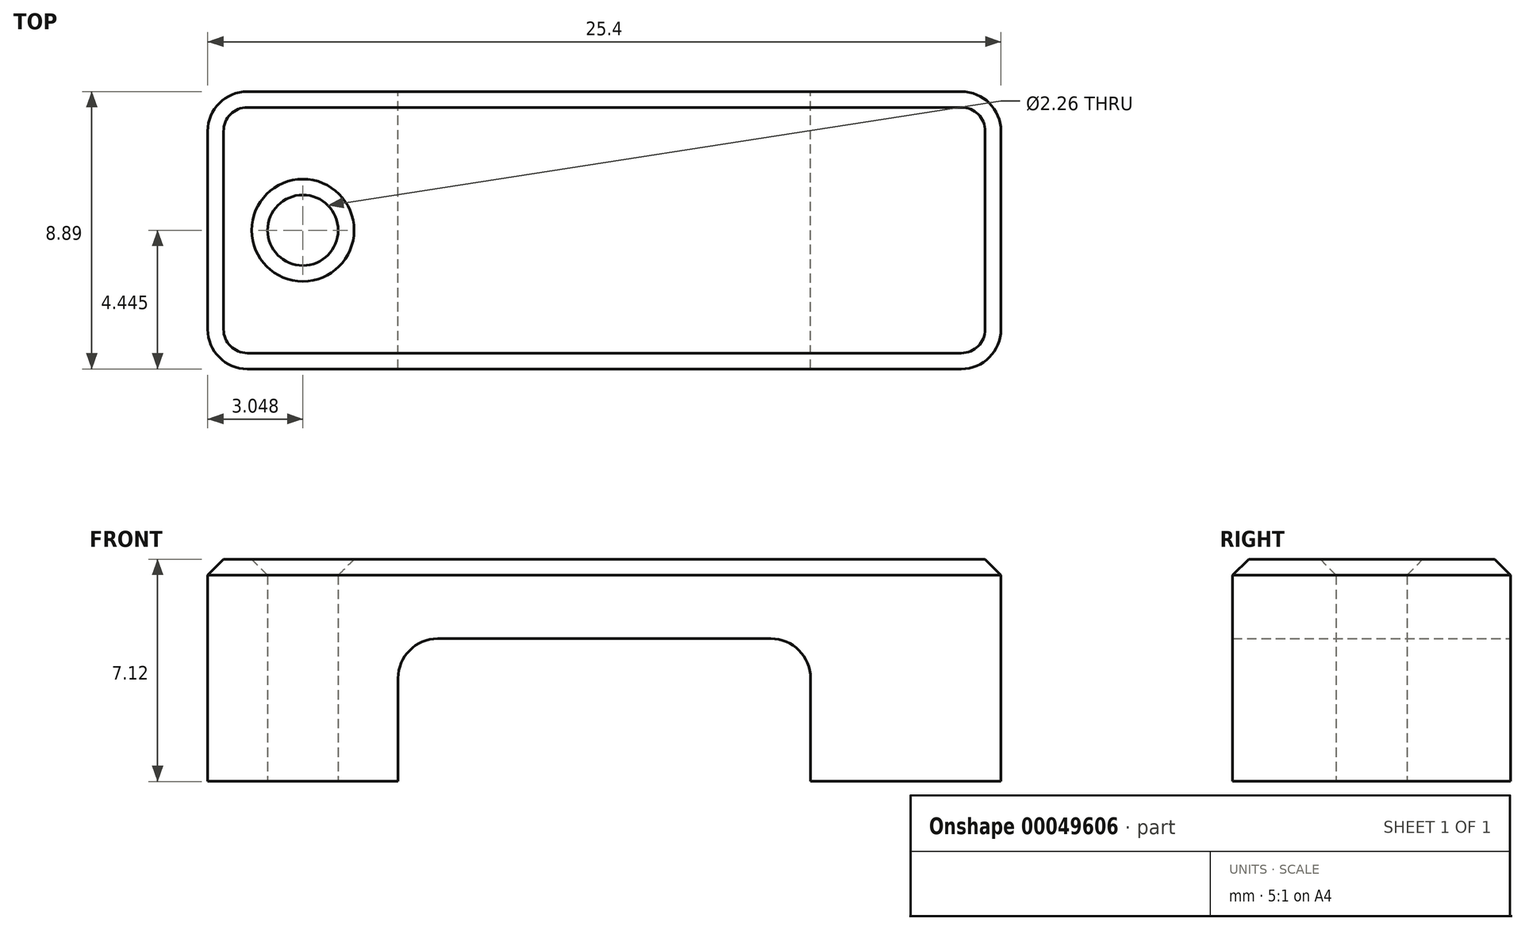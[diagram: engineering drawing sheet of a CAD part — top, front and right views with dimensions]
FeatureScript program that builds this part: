
annotation { "Feature Type Name" : "Feature", "Feature Type Description" : "" }
export const myFeature = defineFeature(function(context is Context, id is Id, definition is map)
    precondition{}
    {
        {
            var Q0;
            Q0=qCreatedBy(makeId("Front.planeOp"),FACE);
            var sketch = newSketch(context, id + "F0", { "sketchPlane" : qUnion([Q0])});
            skLineSegment(sketch, "E0.rect.bottom", {"start": v(6.6, 2.29) * mm, "end": v(-6.6, 2.29) * mm});
            skLineSegment(sketch, "E0.rect.left", {"start": v(6.6, 2.29) * mm, "end": v(6.6, -2.29) * mm});
            skLineSegment(sketch, "E0.rect.right", {"start": v(-6.6, 2.29) * mm, "end": v(-6.6, -2.29) * mm});
            skPoint(sketch, "E0.rect.middle", {"position": v(0, 0) * mm});
            skLineSegment(sketch, "E1.bottom", {"start": v(-12.7, -2.29) * mm, "end": v(-6.6, -2.29) * mm});
            skLineSegment(sketch, "E1.top", {"start": v(-12.7, 4.83) * mm, "end": v(12.7, 4.83) * mm});
            skLineSegment(sketch, "E1.left", {"start": v(-12.7, -2.29) * mm, "end": v(-12.7, 4.83) * mm});
            skLineSegment(sketch, "E1.right", {"start": v(12.7, -2.29) * mm, "end": v(12.7, 4.83) * mm});
            skLineSegment(sketch, "E2.trimOffspring", {"start": v(6.6, -2.29) * mm, "end": v(12.7, -2.29) * mm});
            skSolve(sketch);
        }
        {
            var Q0;
            Q0=makeQuery(id+"F0.imprint","IMPRINT",FACE,{"disambiguationData":[TD([[makeQuery(id+"F0.imprint","IMPRINT",EDGE,{"derivedFrom":sQuery(id+"F0.wireOp",EDGE,"E0.rect.bottom")}),-1.0]])]});
            extrude(context, id + "F1", {"entities" : qUnion([Q0]), "depth" : 8.9 * mm});
        }
        {
            var Q0;
            Q0=makeQuery(id+"F1.opExtrude","SWEPT_FACE",FACE,{"disambiguationData":[OSD([sQuery(id+"F0.wireOp",EDGE,"E1.bottom")])]});
            var sketch = newSketch(context, id + "F2", { "sketchPlane" : qUnion([Q0])});
            skCircle(sketch, "E3", {"center": v(-9.65, 4.45) * mm, "radius": 1.13 * mm});
            skPoint(sketch, "E3.centerSnap0", {"position": v(-12.7, 4.45) * mm});
            skPoint(sketch, "E3.centerSnap1", {"position": v(-9.65, 0) * mm});
            skLineSegment(sketch, "E4", {"start": v(0, -0.56) * mm, "end": v(0, 5.38) * mm, "construction": true});
            skCircle(sketch, "E5.MirrorC", {"center": v(9.65, 4.45) * mm, "radius": 1.13 * mm});
            skSolve(sketch);
        }
        {
            var Q0;
            Q0=makeQuery(id+"F2.imprint","IMPRINT",FACE,{"disambiguationData":[TD([[makeQuery(id+"F2.imprint","IMPRINT",EDGE,{"derivedFrom":sQuery(id+"F2.wireOp",EDGE,"E3")}),1.0]])]});
            var Q1;
            Q1=makeQuery(id+"F2.imprint","IMPRINT",FACE,{"disambiguationData":[TD([[makeQuery(id+"F2.imprint","IMPRINT",EDGE,{"derivedFrom":sQuery(id+"F2.wireOp",EDGE,"E5.MirrorC")}),-1.0]])]});
            extrude(context, id + "F3", {"entities" : qUnion([Q0, Q1]), "operationType" : NewBodyOperationType.REMOVE, "oppositeDirection" : true, "depth" : 25.4 * mm});
        }
        {
            var Q0;
            Q0=makeQuery(id+"F1.opExtrude","SWEPT_EDGE",EDGE,{"disambiguationData":[OSD([sQuery(id+"F0.wireOp",EDGE,"E0.rect.bottom"),sQuery(id+"F0.wireOp",EDGE,"E0.rect.right")])]});
            var Q1;
            Q1=makeQuery(id+"F1.opExtrude","SWEPT_EDGE",EDGE,{"disambiguationData":[OSD([sQuery(id+"F0.wireOp",EDGE,"E0.rect.bottom"),sQuery(id+"F0.wireOp",EDGE,"E0.rect.left")])]});
            var Q2;
            Q2=makeQuery(id+"F1.opExtrude","CAP_EDGE",EDGE,{"disambiguationData":[OSD([sQuery(id+"F0.wireOp",EDGE,"E1.left")])],"isStart":true});
            var Q3;
            Q3=makeQuery(id+"F1.opExtrude","CAP_EDGE",EDGE,{"disambiguationData":[OSD([sQuery(id+"F0.wireOp",EDGE,"E1.left")])],"isStart":false});
            var Q4;
            Q4=makeQuery(id+"F1.opExtrude","CAP_EDGE",EDGE,{"disambiguationData":[OSD([sQuery(id+"F0.wireOp",EDGE,"E1.right")])],"isStart":false});
            var Q5;
            Q5=makeQuery(id+"F1.opExtrude","CAP_EDGE",EDGE,{"disambiguationData":[OSD([sQuery(id+"F0.wireOp",EDGE,"E1.right")])],"isStart":true});
            fillet(context, id + "F4", {"entities" : qUnion([Q0, Q1, Q2, Q3, Q4, Q5]), "radius" : 1.27 * mm, "tangentPropagation" : true, "allowEdgeOverflow" : false});
        }
        {
            var Q0;
            Q0=makeQuery(id+"F1.opExtrude","SWEPT_FACE",FACE,{"disambiguationData":[OSD([sQuery(id+"F0.wireOp",EDGE,"E1.top")])]});
            chamfer(context, id + "F5", {"entities" : qUnion([Q0]), "width" : 0.5 * mm, "tangentPropagation" : true});
        }
    });
